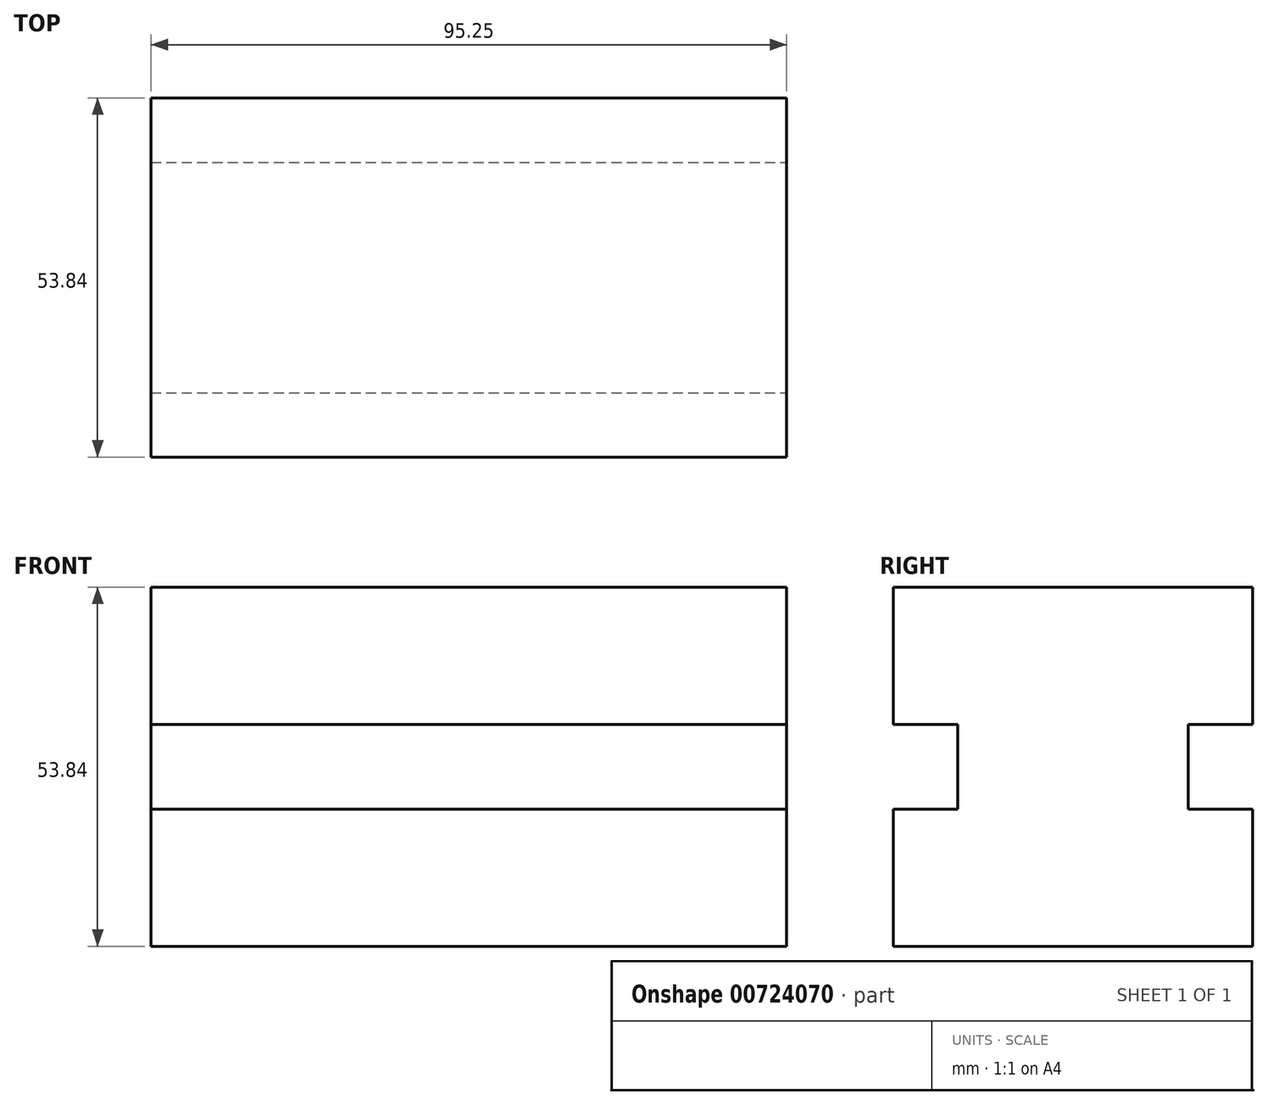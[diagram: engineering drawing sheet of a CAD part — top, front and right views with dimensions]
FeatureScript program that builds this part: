
annotation { "Feature Type Name" : "Feature", "Feature Type Description" : "" }
export const myFeature = defineFeature(function(context is Context, id is Id, definition is map)
    precondition{}
    {
        {
            var Q0;
            Q0=qCreatedBy(makeId("Right.planeOp"),FACE);
            var sketch = newSketch(context, id + "F0", { "sketchPlane" : qUnion([Q0])});
            skLineSegment(sketch, "E0.bottom", {"start": v(26.92, -26.92) * mm, "end": v(-26.92, -26.92) * mm});
            skLineSegment(sketch, "E0.top", {"start": v(26.92, 26.92) * mm, "end": v(-26.92, 26.92) * mm});
            skLineSegment(sketch, "E0.left", {"start": v(26.92, -26.92) * mm, "end": v(26.92, -6.35) * mm});
            skPoint(sketch, "E0.middle", {"position": v(0, 0) * mm});
            skLineSegment(sketch, "E1", {"start": v(-26.92, -26.92) * mm, "end": v(-26.92, -6.35) * mm});
            skLineSegment(sketch, "E2.bottom", {"start": v(-26.92, 6.35) * mm, "end": v(-17.27, 6.35) * mm});
            skLineSegment(sketch, "E2.top", {"start": v(-26.92, -6.35) * mm, "end": v(-17.27, -6.35) * mm});
            skLineSegment(sketch, "E2.right", {"start": v(-17.27, 6.35) * mm, "end": v(-17.27, -6.35) * mm});
            skLineSegment(sketch, "E3.trimOffspring", {"start": v(-26.92, 6.35) * mm, "end": v(-26.92, 26.92) * mm});
            skLineSegment(sketch, "E4", {"start": v(0, 64.08) * mm, "end": v(0, -26.92) * mm, "construction": true});
            skLineSegment(sketch, "E5.MirrorCS", {"start": v(26.92, 6.35) * mm, "end": v(17.27, 6.35) * mm});
            skLineSegment(sketch, "E6.MirrorCS", {"start": v(17.27, 6.35) * mm, "end": v(17.27, -6.35) * mm});
            skLineSegment(sketch, "E7.MirrorCS", {"start": v(26.92, -6.35) * mm, "end": v(17.27, -6.35) * mm});
            skLineSegment(sketch, "E8.trimOffspring", {"start": v(26.92, 6.35) * mm, "end": v(26.92, 26.92) * mm});
            skSolve(sketch);
        }
        {
            var Q0;
            Q0=makeQuery(id+"F0.imprint","IMPRINT",FACE,{"disambiguationData":[TD([[makeQuery(id+"F0.imprint","IMPRINT",EDGE,{"derivedFrom":sQuery(id+"F0.wireOp",EDGE,"E0.bottom")}),-1.0]])]});
            extrude(context, id + "F1", {"entities" : qUnion([Q0]), "oppositeDirection" : true, "depth" : 95.25 * mm, "offsetDistance" : 25.4 * mm});
        }
    });
